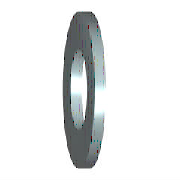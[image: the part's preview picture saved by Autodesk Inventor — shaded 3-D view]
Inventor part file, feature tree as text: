
AUTODESK INVENTOR PART (.ipt)
format: ipt  version: 2015 (Build 190159000, 159)  size: 111,104 bytes
history: native  units: mm (DEFAULTED — no unit token found)
features: other x1, plane x1, sketch x1
ambient origin geometry x7: Origin, YZ Plane, XY Plane, X Axis, Y Axis, Z Axis, Center Point
bodies: Solid1 (feature_tree), Body (feature_tree)
feature tree (3):
  other  "Work Axis1"
  plane  "Work Plane1"
  sketch  "Sketch"  dims[d0=5.3mm d1=10.0mm d2=1.0mm d3=0.0mm d4=0.0mm d5=0.0mm d6=0.0mm d7=0.0mm]
